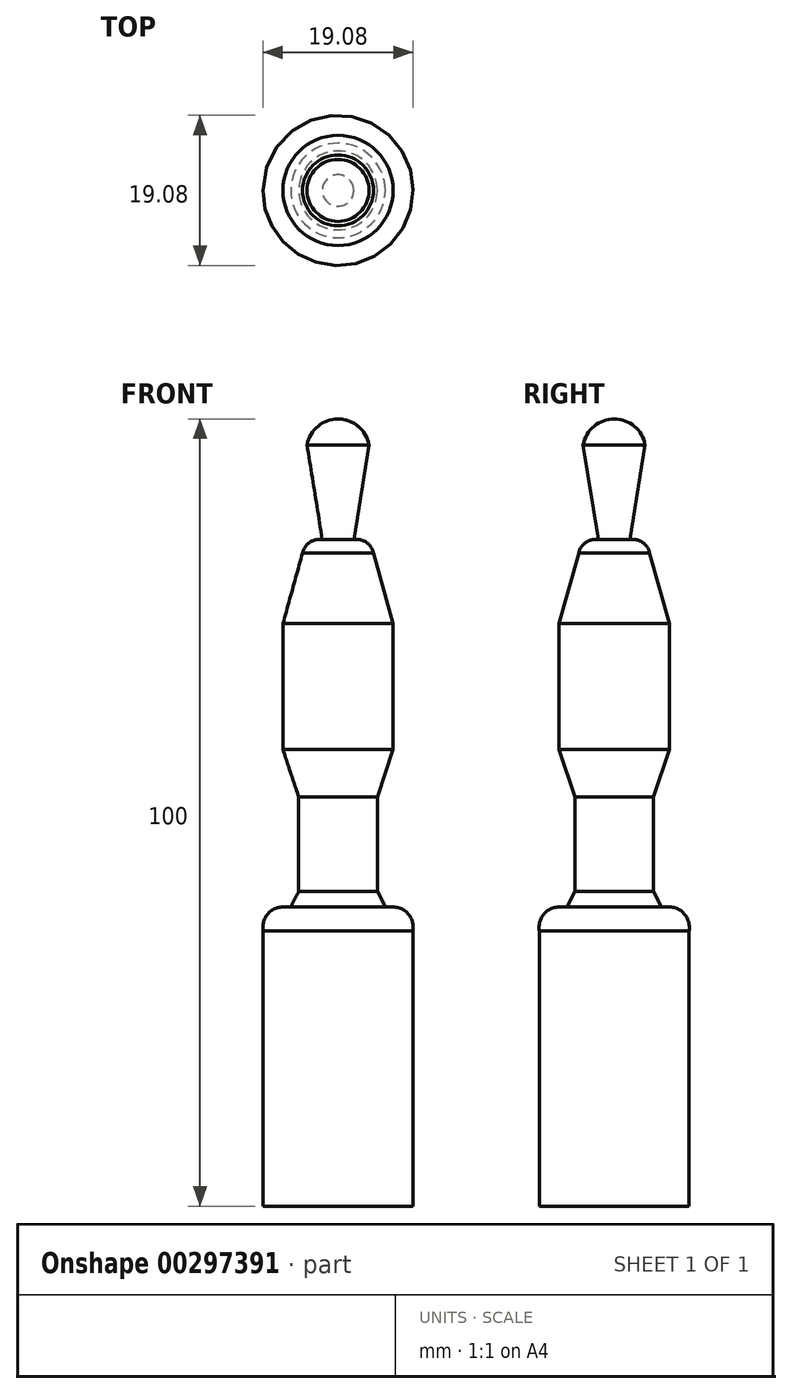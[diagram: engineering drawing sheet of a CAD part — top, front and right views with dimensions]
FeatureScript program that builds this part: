
annotation { "Feature Type Name" : "Feature", "Feature Type Description" : "" }
export const myFeature = defineFeature(function(context is Context, id is Id, definition is map)
    precondition{}
    {
        {
            var Q0;
            Q0=qCreatedBy(makeId("Front.planeOp"),FACE);
            var sketch = newSketch(context, id + "F0", { "sketchPlane" : qUnion([Q0])});
            skArc(sketch, "E0", {"start": v(3.94, -3.3) * mm, "mid": v(2.57, -0.93) * mm, "end": v(0, 0) * mm});
            skLineSegment(sketch, "E1", {"start": v(3.94, -3.3) * mm, "end": v(2, -15.33) * mm});
            skArc(sketch, "E2", {"start": v(4.5, -17) * mm, "mid": v(3.59, -15.66) * mm, "end": v(2, -15.33) * mm});
            skLineSegment(sketch, "E3", {"start": v(4.5, -17) * mm, "end": v(7, -26) * mm});
            skLineSegment(sketch, "E4", {"start": v(7, -26) * mm, "end": v(7, -42) * mm});
            skLineSegment(sketch, "E5", {"start": v(7, -42) * mm, "end": v(5, -48) * mm});
            skLineSegment(sketch, "E6", {"start": v(5, -48) * mm, "end": v(5, -60) * mm});
            skLineSegment(sketch, "E7", {"start": v(5, -60) * mm, "end": v(6, -62) * mm});
            skLineSegment(sketch, "E8", {"start": v(6, -62) * mm, "end": v(7, -62) * mm});
            skArc(sketch, "E9", {"start": v(9.5, -65) * mm, "mid": v(8.95, -62.91) * mm, "end": v(7, -62) * mm});
            skLineSegment(sketch, "E10", {"start": v(9.5, -65) * mm, "end": v(9.5, -100) * mm});
            skLineSegment(sketch, "E11", {"start": v(9.5, -100) * mm, "end": v(0, -100) * mm});
            skLineSegment(sketch, "E12", {"start": v(0, -100) * mm, "end": v(0, 0) * mm});
            skSolve(sketch);
        }
        {
            var Q0;
            Q0 = qSketchRegion(id + "F0", true);
            var Q1;
            Q1=sQuery(id+"F0.wireOp",EDGE,"E12");
            revolve(context, id + "F1", {"entities" : qUnion([Q0]), "axis" : qUnion([Q1]), "revolveType" : RevolveType.FULL});
        }
    });
